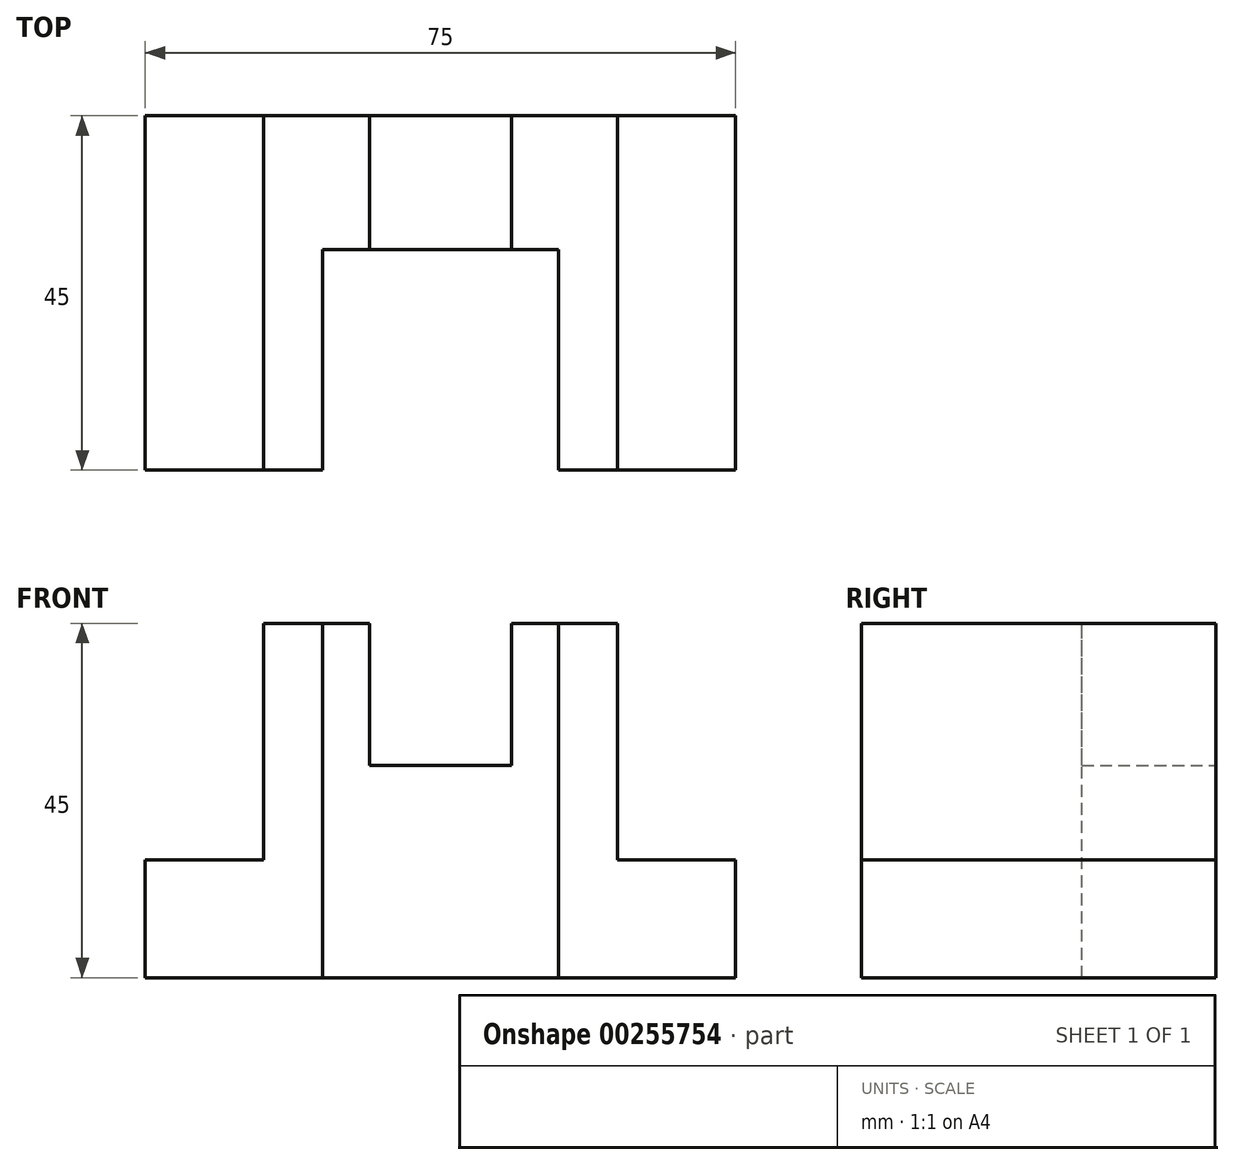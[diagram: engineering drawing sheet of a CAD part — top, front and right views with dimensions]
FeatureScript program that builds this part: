
annotation { "Feature Type Name" : "Feature", "Feature Type Description" : "" }
export const myFeature = defineFeature(function(context is Context, id is Id, definition is map)
    precondition{}
    {
        {
            var Q0;
            Q0=qCreatedBy(makeId("Front.planeOp"),FACE);
            var sketch = newSketch(context, id + "F0", { "sketchPlane" : qUnion([Q0])});
            skLineSegment(sketch, "E0", {"start": v(0, 0) * mm, "end": v(-37.5, 0) * mm});
            skLineSegment(sketch, "E1", {"start": v(-37.5, 0) * mm, "end": v(-37.5, 15) * mm});
            skLineSegment(sketch, "E2", {"start": v(-37.5, 15) * mm, "end": v(-22.5, 15) * mm});
            skLineSegment(sketch, "E3", {"start": v(-22.5, 15) * mm, "end": v(-22.5, 45) * mm});
            skLineSegment(sketch, "E4", {"start": v(-22.5, 45) * mm, "end": v(-9, 45) * mm});
            skLineSegment(sketch, "E5", {"start": v(-9, 45) * mm, "end": v(-9, 27) * mm});
            skLineSegment(sketch, "E6", {"start": v(-9, 27) * mm, "end": v(9, 27) * mm});
            skLineSegment(sketch, "E7", {"start": v(9, 27) * mm, "end": v(9, 45) * mm});
            skLineSegment(sketch, "E8", {"start": v(9, 45) * mm, "end": v(22.5, 45) * mm});
            skLineSegment(sketch, "E9", {"start": v(22.5, 45) * mm, "end": v(22.5, 15) * mm});
            skLineSegment(sketch, "E10", {"start": v(22.5, 15) * mm, "end": v(37.5, 15) * mm});
            skLineSegment(sketch, "E11", {"start": v(37.5, 15) * mm, "end": v(37.5, 0) * mm});
            skLineSegment(sketch, "E12", {"start": v(37.5, 0) * mm, "end": v(0, 0) * mm});
            skSolve(sketch);
        }
        {
            var Q0;
            Q0 = qSketchRegion(id + "F0", true);
            extrude(context, id + "F1", {"entities" : qUnion([Q0]), "depth" : 45 * mm});
        }
        {
            var Q0;
            Q0=makeQuery(id+"F1.opExtrude","SWEPT_FACE",FACE,{"disambiguationData":[OSD([sQuery(id+"F0.wireOp",EDGE,"E4")])]});
            var sketch = newSketch(context, id + "F2", { "sketchPlane" : qUnion([Q0])});
            skLineSegment(sketch, "E13", {"start": v(-15, -45) * mm, "end": v(-15, -17) * mm});
            skLineSegment(sketch, "E14", {"start": v(-15, -17) * mm, "end": v(15, -17) * mm});
            skLineSegment(sketch, "E15", {"start": v(15, -17) * mm, "end": v(15, -45) * mm});
            skLineSegment(sketch, "E16", {"start": v(-15, -45) * mm, "end": v(15, -45) * mm});
            skSolve(sketch);
        }
        {
            var Q0;
            Q0 = qSketchRegion(id + "F2", true);
            extrude(context, id + "F3", {"entities" : qUnion([Q0]), "operationType" : NewBodyOperationType.REMOVE, "endBound" : BoundingType.THROUGH_ALL, "oppositeDirection" : true, "depth" : 25 * mm});
        }
    });
